# Revit family: Toilet_Seat-American_Standard-Advanced_Clean-8017A60GRC-291
name_source: partatom
category: Specialty Equipment
units: mm (PartAtom-declared; Revit-internal decimal feet)

## family parameters
Always vertical = No
Cut with Voids When Loaded = No
OmniClass Number = 23.45.05.21.14.11
OmniClass Title = Water Closet Seats
Part Type = Normal
Room Calculation Point = No
Round Connector Dimension = Use Diameter
Shared = Yes
Work Plane-Based = Yes

## types (1)
- 8017A60GRC-291
    ADA Compliant = Yes
    Assembly Code = C1030200
    Default Elevation = 0"
    Description = Advanced Clean 100 SpaLet Bidet Toilet Seat Unit
    Finish = Plastic-American Standard-291-Alabaster White
    Flush Rate = Dual Flush 1.32 - 0.92 gpf/4.9 - 3.4 Lpf
    Flushing Type = Dual Flush
    Frequency = 60 Hz
    Height = 5 7/16"
    Installation Type = Surface Mounted
    Length = 25 1/16"
    Manufacturer = American Standard
    Material = Plastic-American Standard-291-Alabaster White
    Model = 8017A60GRC-291
    Power Cord Effective Length = 39-3/8" (1.0m)
    Price = Prices may vary. Please consult Manufacturer Representative for most up-to-date price list.
    Product Documentation Link = https://americanstandard.box.com
    Product Page URL = https://www.americanstandard-us.com
    Rated Power Consumption = 1,300 W
    Rated Power Source = 120 VAC, 60 Hz
    Shipping Weight = 12 kg/26>5 lbs
    Type Comments = Auto-Flush: Toilet automatically flushes
    URL = https://www.americanstandard-us.com
    Voltage = 120 V
    Warranty Information = 3 Year Limited Warranty
    Width = 14 3/4"

## geometry (parser evidence)
native form markers: Sweep x2
no freeform markers — native parametric forms only
